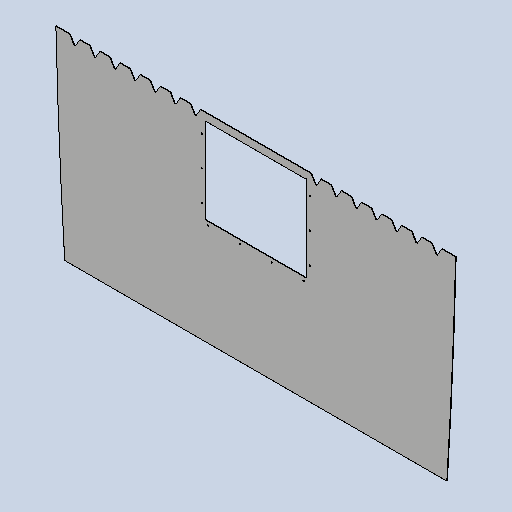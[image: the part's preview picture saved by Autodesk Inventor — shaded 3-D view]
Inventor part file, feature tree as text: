
AUTODESK INVENTOR PART (.ipt)
format: ipt  version: 2025 (Build 290162010, 162A)  size: 425,472 bytes
history: native  units: mm
features: sketch x3, other x2, sheet_metal_op x1, extrude x1, pattern_linear x1, hole x1, mirror x1, projected_geometry x1
ambient origin geometry x8: Origin, YZ Plane, XZ Plane, XY Plane, X Axis, Y Axis, Z Axis, Center Point
bodies: Solid1 (feature_tree)
feature tree (11):
  sheet_metal_op  "Face1"
  extrude  "Extrusion1"  Depth=790.0mm
  pattern_linear  "Rectangular Pattern1"  Count1=20  [1 undecoded]
  sketch  "Sketch7"  dims[d19=370.0mm d23=900.0mm d34=30.0mm d35=5.0mm d36=40.0mm d38=0.0mm d39=0.0mm d40=70.0mm d42=80.0mm d43=30.0mm d44=20.0mm d45=15.0mm d46=240.0mm d47=10.0mm d48=15.0mm d49=190.0mm d50=126.666667mm d51=5.1mm d52=6.0mm d53=4.0mm d54=2.0mm d55=90.0deg d56=2.0mm d57=20.594885mm d58=760.0mm d59=790.0mm d60=795.0mm d61=20475.0mm]
  hole  "Hole1"  [1 undecoded]
  mirror  "Mirror1"
  sketch  "Sketch1"  dims[d0=513.0mm d2=790.0mm]
  other  "Plate1"
  sketch  "Sketch5"  dims[d3=2.0mm d6=200.0mm]
  projected_geometry  "Projected Loop1"
  other  "Definition1"
note: 2 required parameter values undecoded (feature->parameter linkage not recoverable at this tier; creation-order binding heuristic only, values carry confidence <= 0.55)
